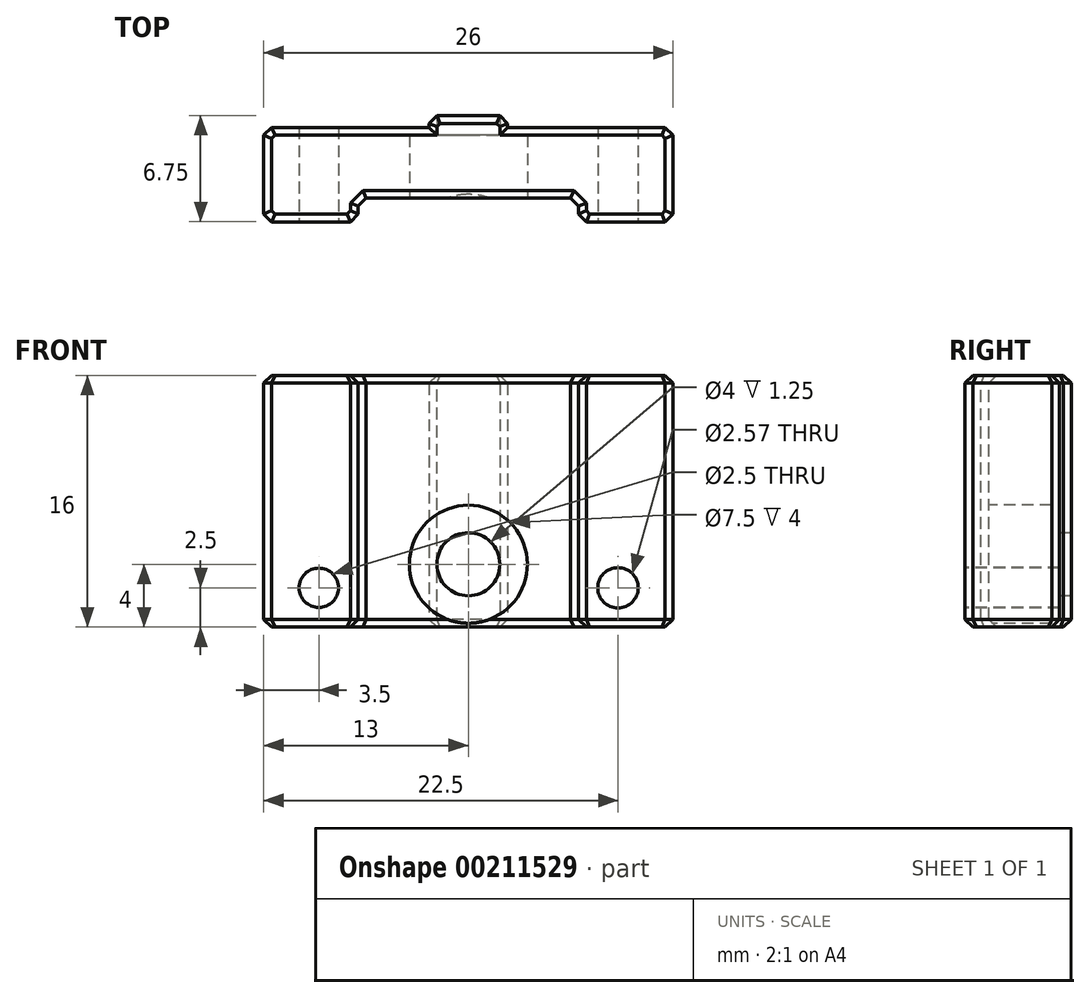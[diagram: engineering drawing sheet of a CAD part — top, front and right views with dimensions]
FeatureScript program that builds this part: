
annotation { "Feature Type Name" : "Feature", "Feature Type Description" : "" }
export const myFeature = defineFeature(function(context is Context, id is Id, definition is map)
    precondition{}
    {
        {
            var Q0;
            Q0=qCreatedBy(makeId("Top.planeOp"),FACE);
            var sketch = newSketch(context, id + "F0", { "sketchPlane" : qUnion([Q0])});
            skLineSegment(sketch, "E0", {"start": v(-13, 3.5) * mm, "end": v(-13, -2.5) * mm});
            skLineSegment(sketch, "E1", {"start": v(-13, -2.5) * mm, "end": v(-7, -2.5) * mm});
            skLineSegment(sketch, "E2", {"start": v(-7, -2.5) * mm, "end": v(-7, -1) * mm});
            skLineSegment(sketch, "E3", {"start": v(-7, -1) * mm, "end": v(7, -1) * mm});
            skLineSegment(sketch, "E4", {"start": v(7, -1) * mm, "end": v(7, -2.5) * mm});
            skLineSegment(sketch, "E5", {"start": v(7, -2.5) * mm, "end": v(13, -2.5) * mm});
            skLineSegment(sketch, "E6", {"start": v(13, -2.5) * mm, "end": v(13, 3.5) * mm});
            skLineSegment(sketch, "E7", {"start": v(13, 3.5) * mm, "end": v(2.5, 3.5) * mm});
            skLineSegment(sketch, "E8", {"start": v(2.5, 3.5) * mm, "end": v(2.5, 4.25) * mm});
            skLineSegment(sketch, "E9", {"start": v(2.5, 4.25) * mm, "end": v(-2.5, 4.25) * mm});
            skLineSegment(sketch, "E10", {"start": v(-2.5, 4.25) * mm, "end": v(-2.5, 3.5) * mm});
            skLineSegment(sketch, "E11", {"start": v(-2.5, 3.5) * mm, "end": v(-13, 3.5) * mm});
            skSolve(sketch);
        }
        {
            var Q0;
            Q0=makeQuery(id+"F0.imprint","IMPRINT",FACE,{"disambiguationData":[TD([[makeQuery(id+"F0.imprint","IMPRINT",EDGE,{"derivedFrom":sQuery(id+"F0.wireOp",EDGE,"E0")}),1.0]])]});
            extrude(context, id + "F1", {"entities" : qUnion([Q0]), "depth" : 16 * mm});
        }
        {
            var Q0;
            Q0=makeQuery(id+"F1.opExtrude","SWEPT_FACE",FACE,{"disambiguationData":[OSD([sQuery(id+"F0.wireOp",EDGE,"E1")])]});
            cPlane(context, id + "F2", {"entities" : qUnion([Q0]), "cplaneType" : CPlaneType.OFFSET, "offset" : 0 * mm, "width" : 150 * mm, "height" : 150 * mm});
        }
        {
            var Q0;
            Q0=qCreatedBy(id+"F2.planeOp",FACE);
            var sketch = newSketch(context, id + "F3", { "sketchPlane" : qUnion([Q0])});
            skCircle(sketch, "E12", {"center": v(-9.5, 2.5) * mm, "radius": 1.25 * mm});
            skCircle(sketch, "E13", {"center": v(9.5, 2.5) * mm, "radius": 1.28 * mm});
            skLineSegment(sketch, "E14", {"start": v(-9.5, 2.5) * mm, "end": v(9.5, 2.5) * mm});
            skSolve(sketch);
        }
        {
            var Q0;
            Q0=makeQuery(id+"F3.imprint","IMPRINT",FACE,{"disambiguationData":[TD([[makeQuery(id+"F3.imprint","IMPRINT",EDGE,{"derivedFrom":sQuery(id+"F3.wireOp",EDGE,"E12")}),1.0]])]});
            var Q1;
            Q1=makeQuery(id+"F3.imprint","IMPRINT",FACE,{"disambiguationData":[TD([[makeQuery(id+"F3.imprint","IMPRINT",EDGE,{"derivedFrom":sQuery(id+"F3.wireOp",EDGE,"E13")}),1.0]])]});
            extrude(context, id + "F4", {"entities" : qUnion([Q0, Q1]), "operationType" : NewBodyOperationType.REMOVE, "oppositeDirection" : true, "depth" : 25 * mm});
        }
        {
            var Q0;
            Q0=makeQuery(id+"F1.opExtrude","SWEPT_FACE",FACE,{"disambiguationData":[OSD([sQuery(id+"F0.wireOp",EDGE,"E3")])]});
            var sketch = newSketch(context, id + "F5", { "sketchPlane" : qUnion([Q0])});
            skCircle(sketch, "E15", {"center": v(0, 4) * mm, "radius": 3.75 * mm});
            skCircle(sketch, "E16", {"center": v(0, 4) * mm, "radius": 2 * mm});
            skSolve(sketch);
        }
        {
            var Q0;
            Q0=makeQuery(id+"F5.imprint","IMPRINT",FACE,{"disambiguationData":[TD([[makeQuery(id+"F5.imprint","IMPRINT",EDGE,{"derivedFrom":sQuery(id+"F5.wireOp",EDGE,"E16")}),1.0]])]});
            extrude(context, id + "F6", {"entities" : qUnion([Q0]), "operationType" : NewBodyOperationType.REMOVE, "oppositeDirection" : true, "depth" : 25 * mm});
        }
        {
            var Q0;
            Q0=makeQuery(id+"F5.imprint","IMPRINT",FACE,{"disambiguationData":[TD([[makeQuery(id+"F5.imprint","IMPRINT",EDGE,{"derivedFrom":sQuery(id+"F5.wireOp",EDGE,"E15")}),1.0]])]});
            extrude(context, id + "F7", {"entities" : qUnion([Q0]), "operationType" : NewBodyOperationType.REMOVE, "oppositeDirection" : true, "depth" : 4 * mm});
        }
        {
            var Q0;
            Q0=makeQuery(id+"F1.opExtrude","SWEPT_EDGE",EDGE,{"disambiguationData":[OSD([sQuery(id+"F0.wireOp",EDGE,"E9"),sQuery(id+"F0.wireOp",EDGE,"E10")])]});
            var Q1;
            Q1=makeQuery(id+"F1.opExtrude","SWEPT_EDGE",EDGE,{"disambiguationData":[OSD([sQuery(id+"F0.wireOp",EDGE,"E8"),sQuery(id+"F0.wireOp",EDGE,"E9")])]});
            var Q2;
            Q2=makeQuery(id+"F1.opExtrude","SWEPT_EDGE",EDGE,{"disambiguationData":[OSD([sQuery(id+"F0.wireOp",EDGE,"E6"),sQuery(id+"F0.wireOp",EDGE,"E7")])]});
            var Q3;
            Q3=makeQuery(id+"F1.opExtrude","SWEPT_EDGE",EDGE,{"disambiguationData":[OSD([sQuery(id+"F0.wireOp",EDGE,"E0"),sQuery(id+"F0.wireOp",EDGE,"E11")])]});
            var Q4;
            Q4=makeQuery(id+"F1.opExtrude","SWEPT_EDGE",EDGE,{"disambiguationData":[OSD([sQuery(id+"F0.wireOp",EDGE,"E0"),sQuery(id+"F0.wireOp",EDGE,"E1")])]});
            var Q5;
            Q5=makeQuery(id+"F1.opExtrude","SWEPT_EDGE",EDGE,{"disambiguationData":[OSD([sQuery(id+"F0.wireOp",EDGE,"E4"),sQuery(id+"F0.wireOp",EDGE,"E5")])]});
            var Q6;
            Q6=makeQuery(id+"F1.opExtrude","SWEPT_EDGE",EDGE,{"disambiguationData":[OSD([sQuery(id+"F0.wireOp",EDGE,"E5"),sQuery(id+"F0.wireOp",EDGE,"E6")])]});
            var Q7;
            Q7=makeQuery(id+"F1.opExtrude","SWEPT_EDGE",EDGE,{"disambiguationData":[OSD([sQuery(id+"F0.wireOp",EDGE,"E1"),sQuery(id+"F0.wireOp",EDGE,"E2")])]});
            var Q8;
            Q8=makeQuery(id+"F1.opExtrude","SWEPT_EDGE",EDGE,{"disambiguationData":[OSD([sQuery(id+"F0.wireOp",EDGE,"E2"),sQuery(id+"F0.wireOp",EDGE,"E3")])]});
            var Q9;
            Q9=makeQuery(id+"F1.opExtrude","SWEPT_EDGE",EDGE,{"disambiguationData":[OSD([sQuery(id+"F0.wireOp",EDGE,"E3"),sQuery(id+"F0.wireOp",EDGE,"E4")])]});
            chamfer(context, id + "F8", {"entities" : qUnion([Q0, Q1, Q2, Q3, Q4, Q5, Q6, Q7, Q8, Q9]), "width" : .5 * mm});
        }
        {
            var Q0;
            Q0=makeQuery(id+"F1.opExtrude","CAP_FACE",FACE,{"disambiguationData":[OSD([sQuery(id+"F0.wireOp",EDGE,"E0"),sQuery(id+"F0.wireOp",EDGE,"E1"),sQuery(id+"F0.wireOp",EDGE,"E2"),sQuery(id+"F0.wireOp",EDGE,"E3"),sQuery(id+"F0.wireOp",EDGE,"E4"),sQuery(id+"F0.wireOp",EDGE,"E5"),sQuery(id+"F0.wireOp",EDGE,"E6"),sQuery(id+"F0.wireOp",EDGE,"E7"),sQuery(id+"F0.wireOp",EDGE,"E8"),sQuery(id+"F0.wireOp",EDGE,"E9"),sQuery(id+"F0.wireOp",EDGE,"E10"),sQuery(id+"F0.wireOp",EDGE,"E11")])],"isStart":false});
            var Q1;
            Q1=makeQuery(id+"F1.opExtrude","CAP_FACE",FACE,{"disambiguationData":[OSD([sQuery(id+"F0.wireOp",EDGE,"E0"),sQuery(id+"F0.wireOp",EDGE,"E1"),sQuery(id+"F0.wireOp",EDGE,"E2"),sQuery(id+"F0.wireOp",EDGE,"E3"),sQuery(id+"F0.wireOp",EDGE,"E4"),sQuery(id+"F0.wireOp",EDGE,"E5"),sQuery(id+"F0.wireOp",EDGE,"E6"),sQuery(id+"F0.wireOp",EDGE,"E7"),sQuery(id+"F0.wireOp",EDGE,"E8"),sQuery(id+"F0.wireOp",EDGE,"E9"),sQuery(id+"F0.wireOp",EDGE,"E10"),sQuery(id+"F0.wireOp",EDGE,"E11")])],"isStart":true});
            chamfer(context, id + "F9", {"entities" : qUnion([Q0, Q1]), "width" : .5 * mm, "tangentPropagation" : true});
        }
    });
